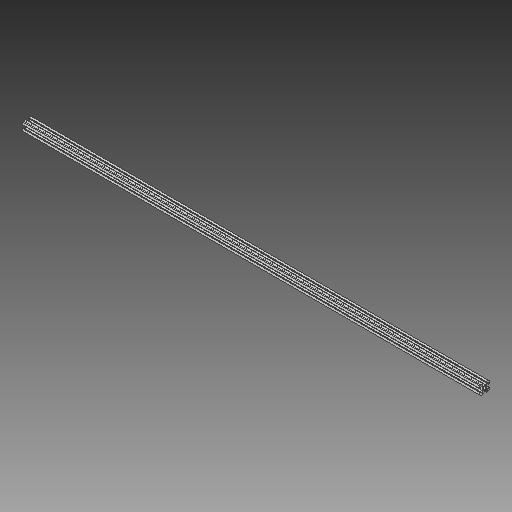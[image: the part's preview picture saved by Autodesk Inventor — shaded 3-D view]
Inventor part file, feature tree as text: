
AUTODESK INVENTOR PART (.ipt)
format: ipt  version: 2019 (Build 230136000, 136)  size: 173,056 bytes
history: native  units: in
note: dims shown in document units (in); Inventor stores cm internally (conversion verified against a paired STEP export)
features: extrude x1, fillet x1, sketch x1
ambient origin geometry x8: Origin, YZ Plane, XZ Plane, XY Plane, X Axis, Y Axis, Z Axis, Center Point
bodies: Solid1 (feature_tree)
feature tree (3):
  extrude  "Extrusion1"  Depth=0.0492in
  fillet  "Fillet1"  [1 undecoded]
  sketch  "Sketch1"  dims[d0=0.1969in d3=0.1417in d4=45.0deg d5=0.122in d7=0.2165in d8=0.063in d11=0.1693in d12=39.3701in d13=0.0in d14=0.0492in]
note: 1 required parameter value undecoded (feature->parameter linkage not recoverable at this tier; creation-order binding heuristic only, values carry confidence <= 0.55)
